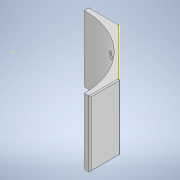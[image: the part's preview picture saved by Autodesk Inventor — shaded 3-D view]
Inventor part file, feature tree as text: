
AUTODESK INVENTOR PART (.ipt)
format: ipt  version: 2021 (Build 250183000, 183)  size: 219,136 bytes
history: native  units: mm
features: sketch x4, extrude x3, other x1, fillet x1
ambient origin geometry x8: Origin, YZ Plane, XZ Plane, XY Plane, X Axis, Y Axis, Z Axis, Center Point
bodies: Body1 (feature_tree)
feature tree (9):
  other  "Sólido1"
  extrude  "Extrusión1"  Depth=2.5mm
  sketch  "Boceto2"  dims[d19=0.5mm d20=1.0mm d21=0.0mm]
  fillet  "Empalme1"  Radius=30.0mm
  extrude  "Extrusión3"  Depth=1.0mm TaperAngle=0.0deg
  extrude  "Extrusión4"  Depth=10.0mm
  sketch  "Boceto1"  dims[d2=2.5mm d3=2.5mm d4=30.0mm d5=0.0mm]
  sketch  "Boceto9"  dims[d37=10.0mm d38=0.0mm d6=0.5mm]
  sketch  "Boceto11"  dims[d7=0.872665mm d22=0.5mm d23=0.872665mm]
